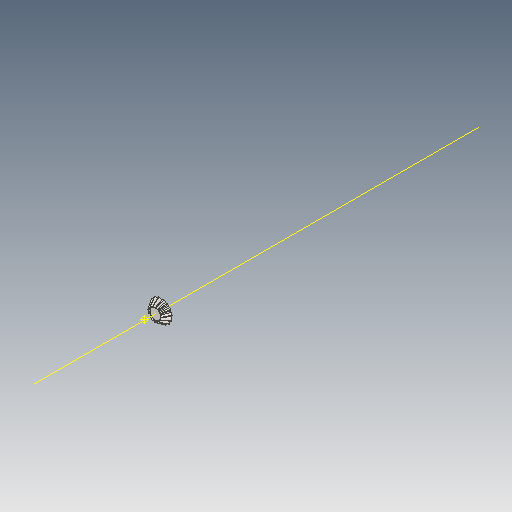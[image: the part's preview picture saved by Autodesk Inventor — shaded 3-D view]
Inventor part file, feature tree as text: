
AUTODESK INVENTOR PART (.ipt)
format: ipt  version: 2021 (Build 250183000, 183)  size: 494,080 bytes
history: native  units: mm
features: other x16, sketch x9, loft x3, pattern_circular x3
ambient origin geometry x6: Origin, XZ Plane, X Axis, Y Axis, Z Axis, Center Point
bodies: Solid1 (feature_tree)
feature tree (31):
  other  "Ponto superior"
  other  "Plano de malha 2"
  other  "Corpo dentado"
  other  "Ponto inicial"
  other  "Plano de dente"
  sketch  "Esboço inicial"  dims[d2=1.673237mm]
  other  "Extremidade"
  loft  "Loft"
  pattern_circular  "Circular Pattern"  [2 undecoded]
  sketch  "Esboço 3D direito"  dims[d3=0.6mm]
  other  "Plano final direito"
  loft  "Transição direita"
  pattern_circular  "Padrão circular direito"  [2 undecoded]
  sketch  "Esboço 3D esquerdo"  dims[d4=1.250028mm]
  other  "Plano final esquerdo"
  loft  "Transição esquerda"
  pattern_circular  "Padrão circular esquerdo"  Count=15 Angle=90.0deg
  other  "Fixar corpo"
  other  "Plano de malha"
  other  "Plano superior"
  sketch  "Esboço de corpo dentado"  dims[d5=90.0deg]
  other  "Plano final"
  sketch  "Esboço final"  dims[d7=0.329584mm]
  other  "Helical Curve Left"
  sketch  "Esboço final esquerdo"  dims[d8=0.374753mm]
  sketch  "Esboço de corpo"  dims[d9=0.716165mm]
  sketch  "Sketch6"  dims[d0=1.5mm d1=1.292115mm]
  other  "Srf1"
  other  "Helical Curve Right"
  sketch  "Esboço final direita"  dims[d11=0.611mm d12=0.195408mm d15=0.222188mm d16=0.424609mm d17=0.0mm d18=90.0deg d19=0.0mm d20=90.0deg d21=150.0mm d22=360.0deg d26=8.972975mm d27=0.529239mm d28=1.5mm d29=-5.232783mm d30=0.195408mm d31=0.222188mm d32=0.424609mm d35=0.0mm d37=0.0mm d39=0.0mm d40=90.0deg d41=150.0mm d42=360.0deg d46=90.0deg d47=90.0deg d48=0.0mm d49=0.0mm d50=90.0deg d51=2.094395mm d52=0.0mm d53=0.0mm d54=0.0mm d56=0.435189mm d57=1.031865mm d58=0.719465mm d59=0.611785mm d60=0.426566mm d61=0.611785mm d62=0.426566mm d65=8.972975mm d66=31.5mm d67=1.5mm d68=-5.232783mm d69=0.529239mm d70=0.222188mm d71=0.424609mm d72=0.195408mm d73=0.426566mm d74=0.611785mm d75=0.0mm d77=0.0mm d79=0.0mm d80=90.0deg d81=150.0mm d82=360.0deg d84=10.0mm d85=20.0mm d86=20.0mm d87=10.0mm d88=0.0mm d89=0.0mm d90=90.0deg d91=90.0deg d92=90.0deg d93=90.0deg]
  other  "Diâmetro do flanco"
note: 4 required parameter values undecoded (feature->parameter linkage not recoverable at this tier; creation-order binding heuristic only, values carry confidence <= 0.55)
